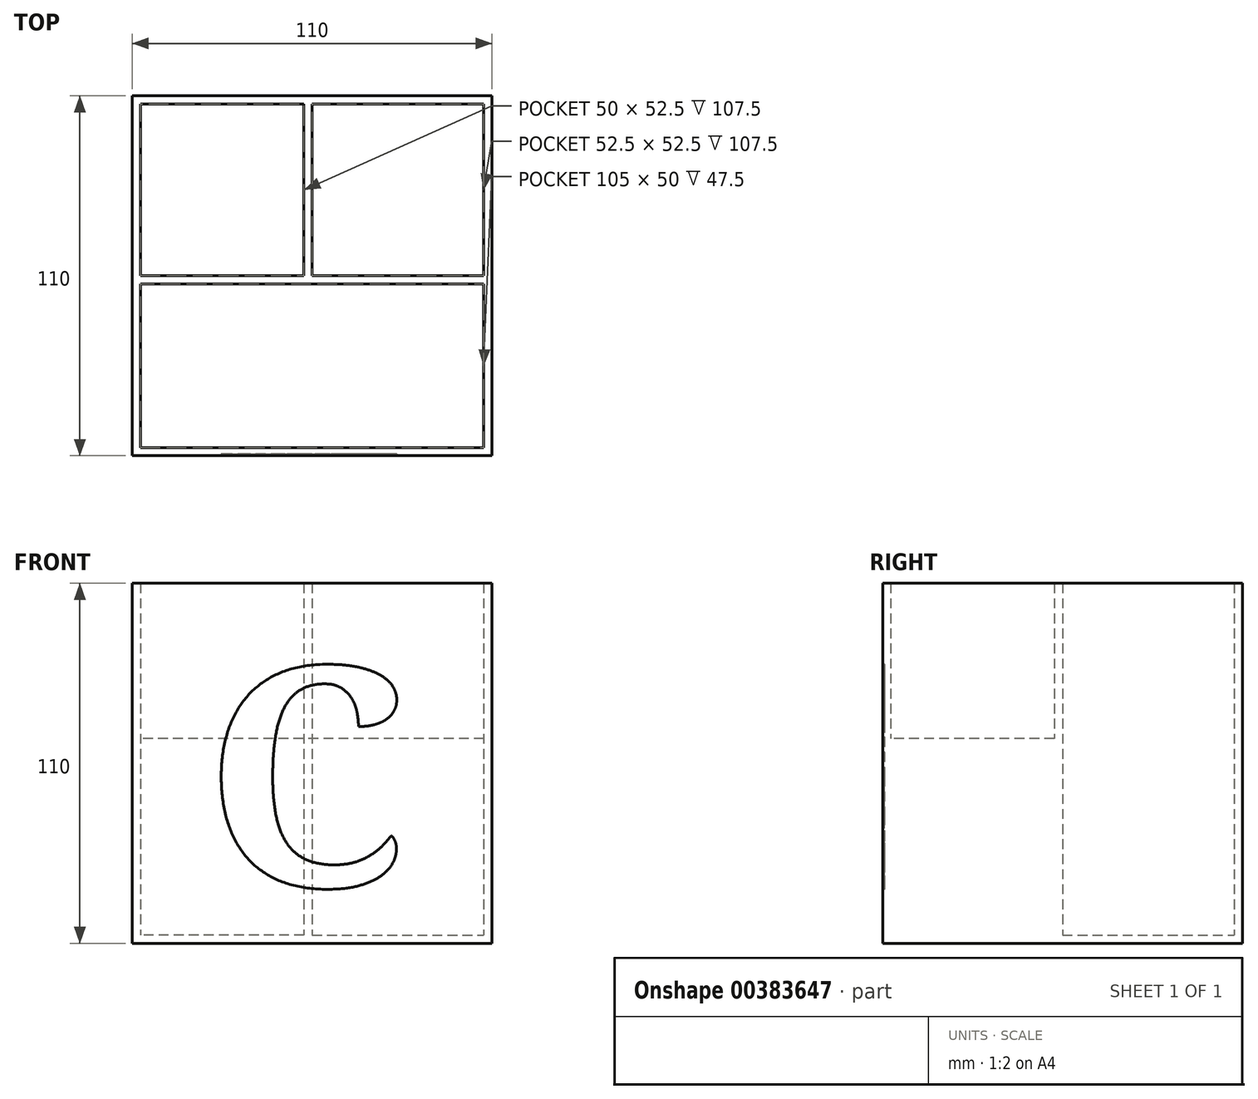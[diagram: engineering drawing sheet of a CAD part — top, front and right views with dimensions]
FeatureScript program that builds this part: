
annotation { "Feature Type Name" : "Feature", "Feature Type Description" : "" }
export const myFeature = defineFeature(function(context is Context, id is Id, definition is map)
    precondition{}
    {
        {
            var Q0;
            Q0=qCreatedBy(makeId("Top.planeOp"),FACE);
            var sketch = newSketch(context, id + "F0", { "sketchPlane" : qUnion([Q0])});
            skLineSegment(sketch, "E0.bottom", {"start": v(0, 0) * mm, "end": v(110, 0) * mm});
            skLineSegment(sketch, "E0.top", {"start": v(0, 110) * mm, "end": v(110, 110) * mm});
            skLineSegment(sketch, "E0.left", {"start": v(0, 0) * mm, "end": v(0, 110) * mm});
            skLineSegment(sketch, "E0.right", {"start": v(110, 0) * mm, "end": v(110, 110) * mm});
            skLineSegment(sketch, "E1.bottom", {"start": v(2.5, 2.5) * mm, "end": v(107.5, 2.5) * mm});
            skLineSegment(sketch, "E1.top", {"start": v(2.5, 52.5) * mm, "end": v(107.5, 52.5) * mm});
            skLineSegment(sketch, "E1.left", {"start": v(2.5, 2.5) * mm, "end": v(2.5, 52.5) * mm});
            skLineSegment(sketch, "E1.right", {"start": v(107.5, 2.5) * mm, "end": v(107.5, 52.5) * mm});
            skLineSegment(sketch, "E2.bottom", {"start": v(107.5, 107.5) * mm, "end": v(55, 107.5) * mm});
            skLineSegment(sketch, "E2.top", {"start": v(107.5, 55) * mm, "end": v(55, 55) * mm});
            skLineSegment(sketch, "E2.left", {"start": v(107.5, 107.5) * mm, "end": v(107.5, 55) * mm});
            skLineSegment(sketch, "E2.right", {"start": v(55, 107.5) * mm, "end": v(55, 55) * mm});
            skLineSegment(sketch, "E3.bottom", {"start": v(2.5, 107.5) * mm, "end": v(52.5, 107.5) * mm});
            skLineSegment(sketch, "E3.top", {"start": v(2.5, 55) * mm, "end": v(52.5, 55) * mm});
            skLineSegment(sketch, "E3.left", {"start": v(2.5, 107.5) * mm, "end": v(2.5, 55) * mm});
            skLineSegment(sketch, "E3.right", {"start": v(52.5, 107.5) * mm, "end": v(52.5, 55) * mm});
            skSolve(sketch);
        }
        {
            var Q0;
            Q0 = qSketchRegion(id + "F0", true);
            extrude(context, id + "F1", {"entities" : qUnion([Q0]), "depth" : 110 * mm});
        }
        {
            var Q0;
            Q0=makeQuery(id+"F1.opExtrude","CAP_FACE",FACE,{"disambiguationData":[OSD([sQuery(id+"F0.wireOp",EDGE,"E0.bottom"),sQuery(id+"F0.wireOp",EDGE,"E0.top"),sQuery(id+"F0.wireOp",EDGE,"E0.left"),sQuery(id+"F0.wireOp",EDGE,"E0.right"),sQuery(id+"F0.wireOp",EDGE,"E1.bottom"),sQuery(id+"F0.wireOp",EDGE,"E1.top"),sQuery(id+"F0.wireOp",EDGE,"E1.left"),sQuery(id+"F0.wireOp",EDGE,"E1.right"),sQuery(id+"F0.wireOp",EDGE,"E2.bottom"),sQuery(id+"F0.wireOp",EDGE,"E2.top"),sQuery(id+"F0.wireOp",EDGE,"E2.left"),sQuery(id+"F0.wireOp",EDGE,"E2.right"),sQuery(id+"F0.wireOp",EDGE,"E3.bottom"),sQuery(id+"F0.wireOp",EDGE,"E3.top"),sQuery(id+"F0.wireOp",EDGE,"E3.left"),sQuery(id+"F0.wireOp",EDGE,"E3.right")])],"isStart":true});
            var sketch = newSketch(context, id + "F2", { "sketchPlane" : qUnion([Q0])});
            skLineSegment(sketch, "E4.bottom", {"start": v(0, 0) * mm, "end": v(110, 0) * mm});
            skLineSegment(sketch, "E4.top", {"start": v(0, -110) * mm, "end": v(110, -110) * mm});
            skLineSegment(sketch, "E4.left", {"start": v(0, 0) * mm, "end": v(0, -110) * mm});
            skLineSegment(sketch, "E4.right", {"start": v(110, 0) * mm, "end": v(110, -110) * mm});
            skSolve(sketch);
        }
        {
            var Q0;
            Q0 = qSketchRegion(id + "F2", true);
            extrude(context, id + "F3", {"entities" : qUnion([Q0]), "operationType" : NewBodyOperationType.ADD, "oppositeDirection" : true, "depth" : 2.5 * mm});
        }
        {
            var Q0;
            Q0=makeQuery(id+"F3.boolean.opBoolean","SPLIT",FACE,{"disambiguationData":[TD([makeQuery(id+"F1.opExtrude","SWEPT_FACE",FACE,{"disambiguationData":[OSD([sQuery(id+"F0.wireOp",EDGE,"E1.bottom")])]})])],"derivedFrom":makeQuery(id+"F3.opExtrude","CAP_FACE",FACE,{"disambiguationData":[OSD([sQuery(id+"F2.wireOp",EDGE,"E4.bottom"),sQuery(id+"F2.wireOp",EDGE,"E4.top"),sQuery(id+"F2.wireOp",EDGE,"E4.left"),sQuery(id+"F2.wireOp",EDGE,"E4.right")])],"isStart":false})});
            extrude(context, id + "F4", {"entities" : qUnion([Q0]), "operationType" : NewBodyOperationType.ADD, "depth" : 60 * mm});
        }
        {
            var Q0;
            Q0=makeQuery(id+"F1.opExtrude","SWEPT_FACE",FACE,{"disambiguationData":[OSD([sQuery(id+"F0.wireOp",EDGE,"E0.bottom")])]});
            var sketch = newSketch(context, id + "F5", { "sketchPlane" : qUnion([Q0])});
            skText(sketch, "E5", { "text": "C", "fontName": "NotoSerif-Bold.ttf"});
            const initialGuessF5  = {"E5": [0.02204, 0.01742, 1, 0, 0.06747]};
            skSetInitialGuess(sketch, initialGuessF5);
            skSolve(sketch);
        }
        {
            var Q0;
            Q0 = qSketchRegion(id + "F5", true);
            extrude(context, id + "F6", {"entities" : qUnion([Q0]), "operationType" : NewBodyOperationType.REMOVE, "oppositeDirection" : true, "depth" : .5 * mm});
        }
    });
